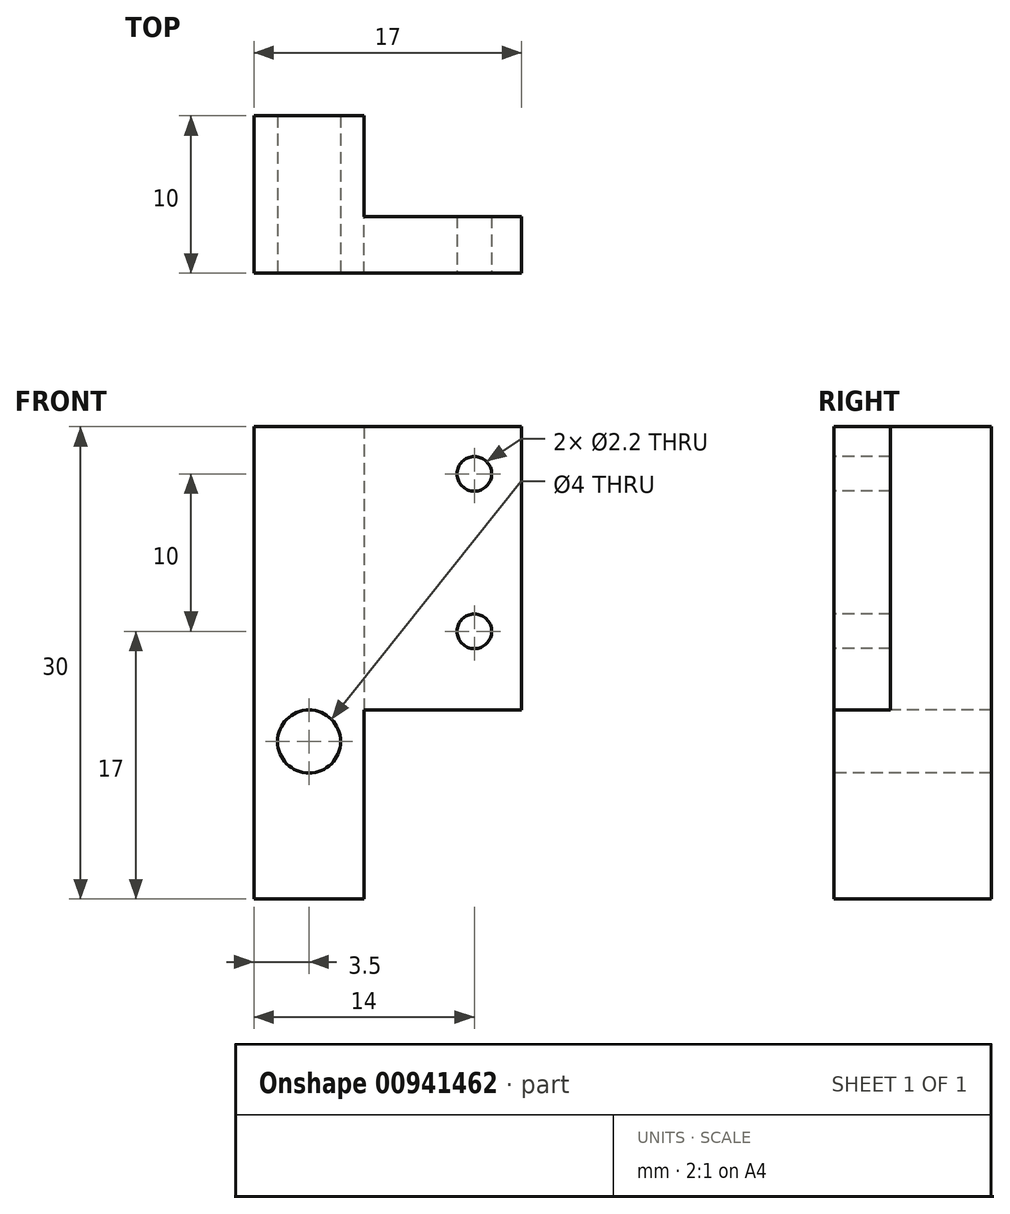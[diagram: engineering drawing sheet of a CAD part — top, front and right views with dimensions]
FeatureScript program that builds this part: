
annotation { "Feature Type Name" : "Feature", "Feature Type Description" : "" }
export const myFeature = defineFeature(function(context is Context, id is Id, definition is map)
    precondition{}
    {
        {
            var Q0;
            Q0=qCreatedBy(makeId("Front.planeOp"),FACE);
            var sketch = newSketch(context, id + "F0", { "sketchPlane" : qUnion([Q0])});
            skLineSegment(sketch, "E0.bottom", {"start": v(0, 0) * mm, "end": v(-17, 0) * mm});
            skLineSegment(sketch, "E0.top", {"start": v(0, -30) * mm, "end": v(-17, -30) * mm});
            skLineSegment(sketch, "E0.left", {"start": v(0, 0) * mm, "end": v(0, -30) * mm});
            skLineSegment(sketch, "E0.right", {"start": v(-17, 0) * mm, "end": v(-17, -30) * mm});
            skSolve(sketch);
        }
        {
            var Q0;
            Q0=makeQuery(id+"F0.imprint","IMPRINT",FACE,{"disambiguationData":[TD([[makeQuery(id+"F0.imprint","IMPRINT",EDGE,{"derivedFrom":sQuery(id+"F0.wireOp",EDGE,"E0.bottom")}),1.0]])]});
            extrude(context, id + "F1", {"entities" : qUnion([Q0]), "depth" : 10 * mm, "offsetDistance" : 25 * mm});
        }
        {
            var Q0;
            Q0=makeQuery(id+"F1.opExtrude","CAP_FACE",FACE,{"disambiguationData":[OSD([sQuery(id+"F0.wireOp",EDGE,"E0.bottom"),sQuery(id+"F0.wireOp",EDGE,"E0.top"),sQuery(id+"F0.wireOp",EDGE,"E0.left"),sQuery(id+"F0.wireOp",EDGE,"E0.right")])],"isStart":true});
            var sketch = newSketch(context, id + "F2", { "sketchPlane" : qUnion([Q0])});
            skLineSegment(sketch, "E1.bottom", {"start": v(0, 0) * mm, "end": v(10, 0) * mm});
            skLineSegment(sketch, "E1.top", {"start": v(0, -30) * mm, "end": v(10, -30) * mm});
            skLineSegment(sketch, "E1.left", {"start": v(0, 0) * mm, "end": v(0, -30) * mm});
            skLineSegment(sketch, "E1.right", {"start": v(10, 0) * mm, "end": v(10, -30) * mm});
            skSolve(sketch);
        }
        {
            var Q0;
            Q0=makeQuery(id+"F2.imprint","IMPRINT",FACE,{"disambiguationData":[TD([[makeQuery(id+"F2.imprint","IMPRINT",EDGE,{"derivedFrom":sQuery(id+"F2.wireOp",EDGE,"E1.bottom")}),-1.0]])]});
            extrude(context, id + "F3", {"entities" : qUnion([Q0]), "operationType" : NewBodyOperationType.REMOVE, "oppositeDirection" : true, "depth" : 6.4 * mm, "offsetDistance" : 25 * mm});
        }
        {
            var Q0;
            Q0=makeQuery(id+"F1.opExtrude","CAP_FACE",FACE,{"disambiguationData":[OSD([sQuery(id+"F0.wireOp",EDGE,"E0.bottom"),sQuery(id+"F0.wireOp",EDGE,"E0.top"),sQuery(id+"F0.wireOp",EDGE,"E0.left"),sQuery(id+"F0.wireOp",EDGE,"E0.right")])],"isStart":false});
            var sketch = newSketch(context, id + "F4", { "sketchPlane" : qUnion([Q0])});
            skCircle(sketch, "E2", {"center": v(-13.5, -20) * mm, "radius": 2 * mm});
            skPoint(sketch, "E2.centerSnap0", {"position": v(-17.5, -20) * mm});
            skSolve(sketch);
        }
        {
            var Q0;
            Q0=makeQuery(id+"F4.imprint","IMPRINT",FACE,{"disambiguationData":[TD([[makeQuery(id+"F4.imprint","IMPRINT",EDGE,{"derivedFrom":sQuery(id+"F4.wireOp",EDGE,"E2")}),1.0]])]});
            extrude(context, id + "F5", {"entities" : qUnion([Q0]), "operationType" : NewBodyOperationType.REMOVE, "oppositeDirection" : true, "depth" : 25 * mm, "offsetDistance" : 25 * mm});
        }
        {
            var Q0;
            Q0=makeQuery(id+"F1.opExtrude","CAP_FACE",FACE,{"disambiguationData":[OSD([sQuery(id+"F0.wireOp",EDGE,"E0.bottom"),sQuery(id+"F0.wireOp",EDGE,"E0.top"),sQuery(id+"F0.wireOp",EDGE,"E0.left"),sQuery(id+"F0.wireOp",EDGE,"E0.right")])],"isStart":false});
            var sketch = newSketch(context, id + "F6", { "sketchPlane" : qUnion([Q0])});
            skCircle(sketch, "E3", {"center": v(-3, -3) * mm, "radius": 1.1 * mm});
            skCircle(sketch, "E4", {"center": v(-3, -13) * mm, "radius": 1.1 * mm});
            skSolve(sketch);
        }
        {
            var Q0;
            Q0=makeQuery(id+"F6.imprint","IMPRINT",FACE,{"disambiguationData":[TD([[makeQuery(id+"F6.imprint","IMPRINT",EDGE,{"derivedFrom":sQuery(id+"F6.wireOp",EDGE,"E3")}),1.0]])]});
            var Q1;
            Q1=makeQuery(id+"F6.imprint","IMPRINT",FACE,{"disambiguationData":[TD([[makeQuery(id+"F6.imprint","IMPRINT",EDGE,{"derivedFrom":sQuery(id+"F6.wireOp",EDGE,"E4")}),1.0]])]});
            extrude(context, id + "F7", {"entities" : qUnion([Q0, Q1]), "operationType" : NewBodyOperationType.REMOVE, "oppositeDirection" : true, "depth" : 25 * mm, "offsetDistance" : 25 * mm});
        }
        {
            var Q0;
            Q0=makeQuery(id+"F3.boolean.opBoolean","COPY",FACE,{"derivedFrom":makeQuery(id+"F3.opExtrude","CAP_FACE",FACE,{"disambiguationData":[OSD([sQuery(id+"F2.wireOp",EDGE,"E1.bottom"),sQuery(id+"F2.wireOp",EDGE,"E1.top"),sQuery(id+"F2.wireOp",EDGE,"E1.left"),sQuery(id+"F2.wireOp",EDGE,"E1.right")])],"isStart":false})});
            var sketch = newSketch(context, id + "F8", { "sketchPlane" : qUnion([Q0])});
            skLineSegment(sketch, "E5.bottom", {"start": v(0, -30) * mm, "end": v(10, -30) * mm});
            skLineSegment(sketch, "E5.top", {"start": v(0, -18) * mm, "end": v(10, -18) * mm});
            skLineSegment(sketch, "E5.left", {"start": v(0, -30) * mm, "end": v(0, -18) * mm});
            skLineSegment(sketch, "E5.right", {"start": v(10, -30) * mm, "end": v(10, -18) * mm});
            skSolve(sketch);
        }
        {
            var Q0;
            Q0=makeQuery(id+"F8.imprint","IMPRINT",FACE,{"disambiguationData":[TD([[makeQuery(id+"F8.imprint","IMPRINT",EDGE,{"derivedFrom":sQuery(id+"F8.wireOp",EDGE,"E5.bottom")}),1.0]])]});
            extrude(context, id + "F9", {"entities" : qUnion([Q0]), "operationType" : NewBodyOperationType.REMOVE, "oppositeDirection" : true, "depth" : 25 * mm, "offsetDistance" : 25 * mm});
        }
    });
